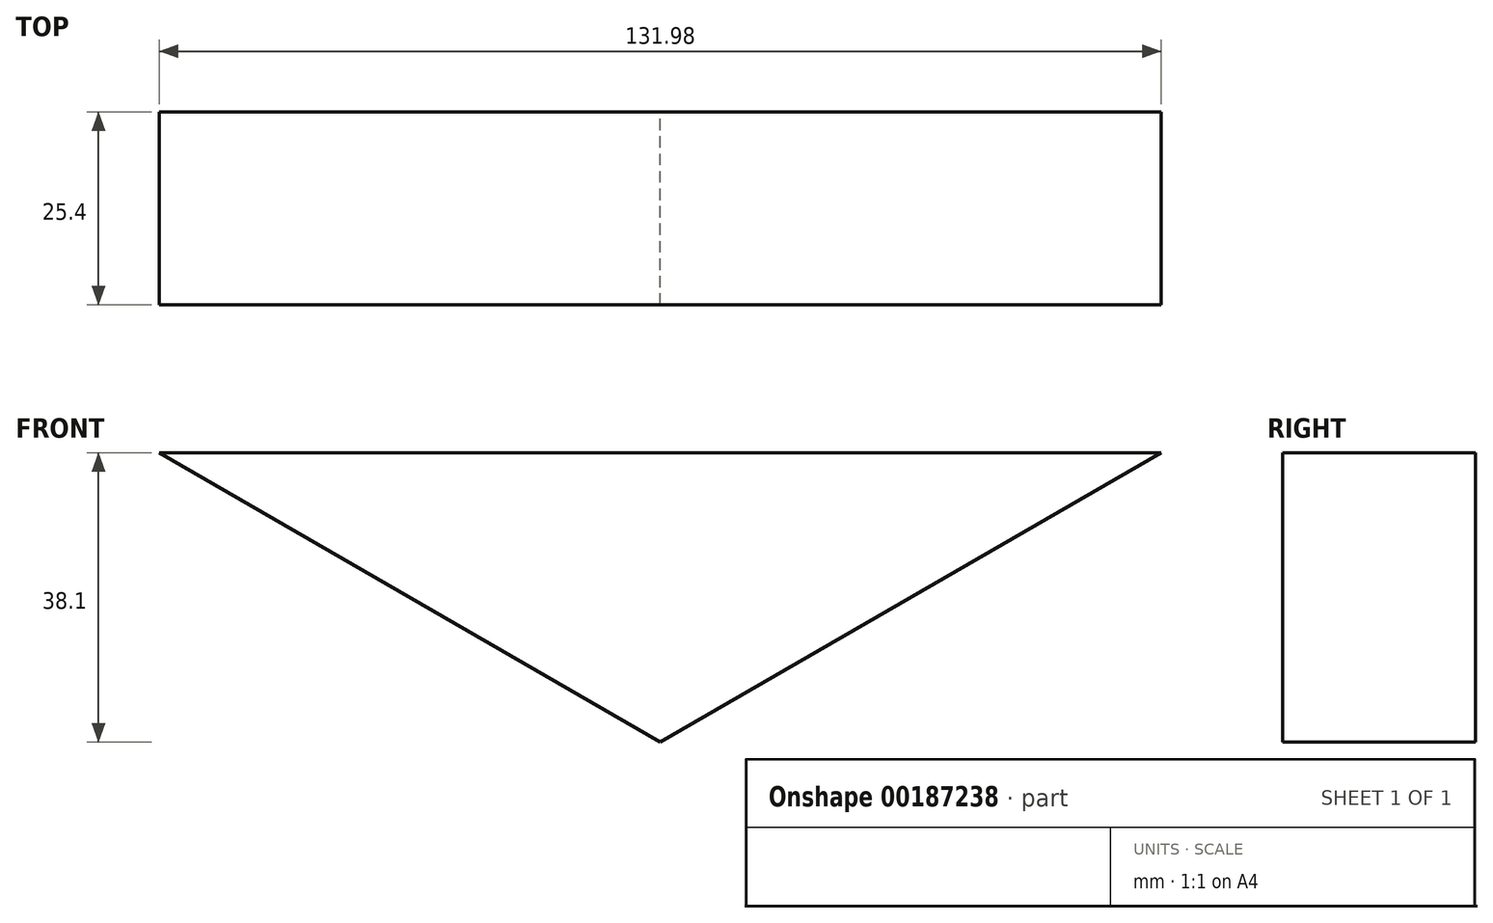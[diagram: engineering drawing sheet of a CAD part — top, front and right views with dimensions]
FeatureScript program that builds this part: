
annotation { "Feature Type Name" : "Feature", "Feature Type Description" : "" }
export const myFeature = defineFeature(function(context is Context, id is Id, definition is map)
    precondition{}
    {
        {
            var Q0;
            Q0=qCreatedBy(makeId("Front.planeOp"),FACE);
            var sketch = newSketch(context, id + "F0", { "sketchPlane" : qUnion([Q0])});
            skLineSegment(sketch, "E0", {"start": v(-66, 38.1) * mm, "end": v(66, 38.1) * mm});
            skLineSegment(sketch, "E1", {"start": v(0, 0) * mm, "end": v(-66, 38.1) * mm});
            skLineSegment(sketch, "E2", {"start": v(0, 0) * mm, "end": v(66, 38.1) * mm});
            skLineSegment(sketch, "E3", {"start": v(0, 0) * mm, "end": v(0, 38.1) * mm});
            skSolve(sketch);
        }
        {
            var Q0;
            {var subQ0=sQuery(id+"F0.wireOp",EDGE,"E2");Q0=makeQuery(id+"F0.imprint","IMPRINT",FACE,{"disambiguationData":[TD([[makeQuery(id+"F0.imprint","IMPRINT",EDGE,{"derivedFrom":subQ0}),1.0]])]});}
            var Q1;
            {var subQ0=sQuery(id+"F0.wireOp",EDGE,"E1");Q1=makeQuery(id+"F0.imprint","IMPRINT",FACE,{"disambiguationData":[TD([[makeQuery(id+"F0.imprint","IMPRINT",EDGE,{"derivedFrom":subQ0}),-1.0]])]});}
            extrude(context, id + "F1", {"entities" : qUnion([Q0, Q1]), "depth" : 25.4 * mm});
        }
    });
